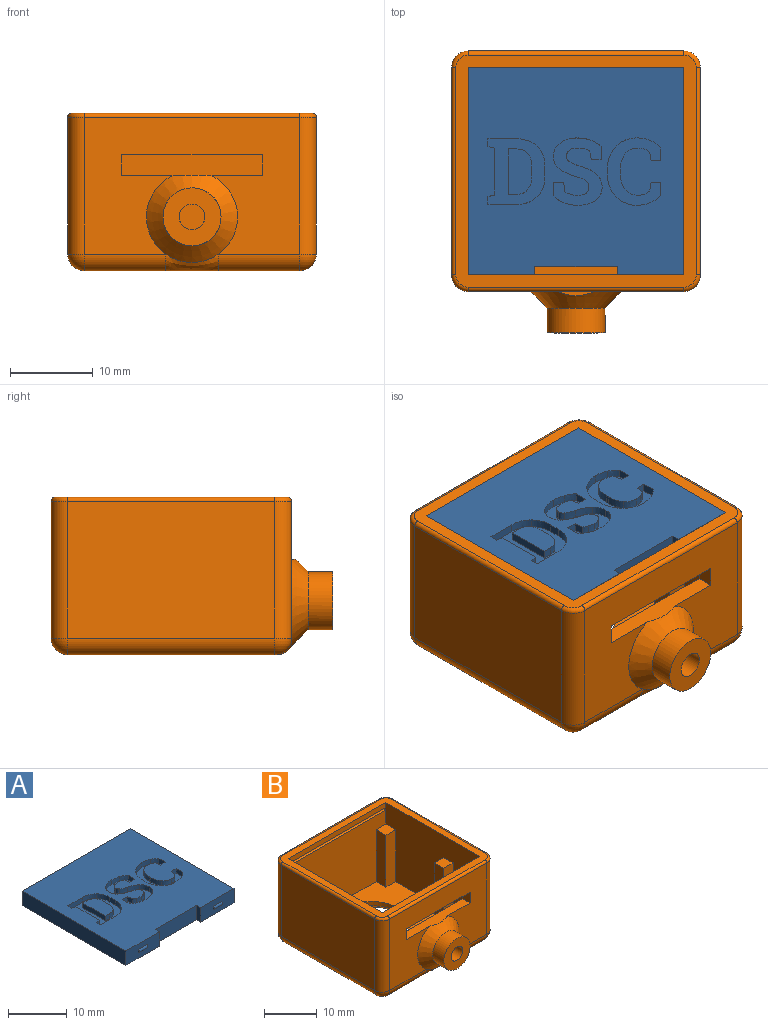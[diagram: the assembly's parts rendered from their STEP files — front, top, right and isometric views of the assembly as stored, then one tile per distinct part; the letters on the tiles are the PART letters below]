
ASSEMBLY  parts=2 mates=1
PART A: 100 faces, bbox 26x25.6x3 mm
  f0: plane 26x25mm, normal (0,0,1), area 544.6mm2, adj f1,f2,f3,f4,f5,f6,f7,f8
  f1: plane 3x1mm, normal (1,0,0), area 3mm2, adj f0,f2,f8,f9
  f2: plane 10x3mm, normal (0,-1,0), area 30mm2, adj f0,f1,f3,f9
  f3: plane 3x1mm, normal (-1,0,0), area 3mm2, adj f0,f2,f4,f9
  f4: plane 8x3mm, normal (0,-1,0), area 22.8mm2, adj f0,f3,f5,f9,f97,f98,f99
  f5: plane 25x3mm, normal (1,0,0), area 75mm2, adj f0,f4,f6,f9
  f6: plane 26x3mm, normal (0,1,0), area 69.6mm2, adj f0,f5,f7,f9,f88,f89,f90,f91
  f7: plane 25x3mm, normal (-1,0,0), area 75mm2, adj f0,f6,f8,f9
  f8: plane 8x3mm, normal (0,-1,0), area 22.8mm2, adj f0,f1,f7,f9,f94,f95,f96
  f9: plane 26x25mm, normal (0,0,-1), area 640mm2, adj f1,f2,f3,f4,f5,f6,f7,f8
  f10: plane 1.62x1mm, normal (-1,0,0), area 1.6mm2, adj f0,f11,f39,f40
  f11: extruded ~1.26x1mm, area 1.5mm2, adj f0,f10,f12,f40
  f12: extruded ~1.66x1mm, area 1.7mm2, adj f0,f11,f13,f40
  f13: extruded ~2.05x1mm, area 2.2mm2, adj f0,f12,f14,f40
  f14: extruded ~1.57x1mm, area 1.8mm2, adj f0,f13,f15,f40
  f15: extruded ~1.53x1mm, area 1.8mm2, adj f0,f14,f16,f40
  f16: extruded ~2.13x1mm, area 2.4mm2, adj f0,f15,f17,f40
  f17: extruded ~1.13x1mm, area 1.3mm2, adj f0,f16,f18,f40
  f18: extruded ~1x0.73mm, area 0.8mm2, adj f0,f17,f19,f40
  f19: extruded ~1x0.71mm, area 0.8mm2, adj f0,f18,f20,f40
  f20: extruded ~1x0.99mm, area 1mm2, adj f0,f19,f21,f40
  f21: extruded ~1x0.92mm, area 0.9mm2, adj f0,f20,f22,f40
  f22: extruded ~1x0.65mm, area 0.7mm2, adj f0,f21,f23,f40
  f23: plane 1.12x1mm, normal (-0.99,-0.15,0), area 1.1mm2, adj f0,f22,f24,f40
  f24: plane 1.23x1mm, normal (0,-1,0), area 1.2mm2, adj f0,f23,f25,f40
  f25: plane 1.65x1mm, normal (1,0,0), area 1.6mm2, adj f0,f24,f26,f40
  f26: extruded ~1.26x1mm, area 1.5mm2, adj f0,f25,f27,f40
  f27: extruded ~1.7x1mm, area 1.7mm2, adj f0,f26,f28,f40
  f28: extruded ~2.12x1mm, area 2.2mm2, adj f0,f27,f29,f40
  f29: extruded ~1.6x1mm, area 1.9mm2, adj f0,f28,f30,f40
  f30: extruded ~1.57x1mm, area 1.8mm2, adj f0,f29,f31,f40
  f31: extruded ~1.98x1mm, area 2.2mm2, adj f0,f30,f32,f40
  f32: extruded ~1.28x1mm, area 1.4mm2, adj f0,f31,f33,f40
  f33: extruded ~1x0.66mm, area 0.8mm2, adj f0,f32,f34,f40
  f34: extruded ~1x0.71mm, area 0.8mm2, adj f0,f33,f35,f40
  f35: extruded ~1.01x1mm, area 1.1mm2, adj f0,f34,f36,f40
  f36: extruded ~1x0.84mm, area 0.8mm2, adj f0,f35,f37,f40
  f37: extruded ~1x0.6mm, area 0.6mm2, adj f0,f36,f38,f40
  f38: plane 1.09x1mm, normal (0.98,0.19,0), area 1.1mm2, adj f0,f37,f39,f40
  f39: plane 1.19x1mm, normal (0,1,0), area 1.2mm2, adj f0,f10,f38,f40
  f40: plane 8.12x5.89mm, normal (0,0,1), area 26.6mm2, adj f10,f11,f12,f13,f14,f15,f16,f17
  f41: plane 1.56x1mm, normal (-1,0,0), area 1.6mm2, adj f0,f42,f64,f65
  f42: extruded ~1.22x1mm, area 1.5mm2, adj f0,f41,f43,f65
  f43: extruded ~1.65x1mm, area 1.7mm2, adj f0,f42,f44,f65
  f44: extruded ~2.61x1.11mm, area 2.9mm2, adj f0,f43,f45,f65
  f45: extruded ~2.83x1.01mm, area 3.1mm2, adj f0,f44,f46,f65
  f46: plane 1x0.27mm, normal (1,0,0), area 0.3mm2, adj f0,f45,f47,f65
  f47: extruded ~2.83x1.01mm, area 3.1mm2, adj f0,f46,f48,f65
  f48: extruded ~2.6x1.1mm, area 2.9mm2, adj f0,f47,f49,f65
  f49: extruded ~1.66x1mm, area 1.7mm2, adj f0,f48,f50,f65
  f50: extruded ~1.22x1mm, area 1.5mm2, adj f0,f49,f51,f65
  f51: plane 1.56x1mm, normal (-1,0,0), area 1.6mm2, adj f0,f50,f52,f65
  f52: plane 1.18x1mm, normal (0,-1,0), area 1.2mm2, adj f0,f51,f53,f65
  f53: plane 1.05x1mm, normal (0.99,-0.15,0), area 1.1mm2, adj f0,f52,f54,f65
  f54: extruded ~1x0.6mm, area 0.7mm2, adj f0,f53,f55,f65
  f55: extruded ~1x0.85mm, area 0.9mm2, adj f0,f54,f56,f65
  f56: extruded ~1.56x1mm, area 1.8mm2, adj f0,f55,f57,f65
  f57: extruded ~1.96x1mm, area 2.1mm2, adj f0,f56,f58,f65
  f58: plane 1x0.28mm, normal (-1,0,0), area 0.3mm2, adj f0,f57,f59,f65
  f59: extruded ~1.95x1mm, area 2.1mm2, adj f0,f58,f60,f65
  f60: extruded ~1.59x1mm, area 1.8mm2, adj f0,f59,f61,f65
  f61: extruded ~1x0.84mm, area 0.9mm2, adj f0,f60,f62,f65
  f62: extruded ~1x0.59mm, area 0.7mm2, adj f0,f61,f63,f65
  f63: plane 1.05x1mm, normal (0.99,0.15,0), area 1.1mm2, adj f0,f62,f64,f65
  f64: plane 1.18x1mm, normal (0,1,0), area 1.2mm2, adj f0,f41,f63,f65
  f65: plane 8.13x6.49mm, normal (0,0,1), area 23.7mm2, adj f41,f42,f43,f44,f45,f46,f47,f48
  f66: plane 3.55x1mm, normal (0,-1,0), area 3.6mm2, adj f0,f67,f85,f86
  f67: plane 1x0.96mm, normal (1,0,0), area 1mm2, adj f0,f66,f68,f86
  f68: plane 1x0.84mm, normal (0.19,0.98,0), area 0.9mm2, adj f0,f67,f69,f86
  f69: plane 5.67x1mm, normal (1,0,0), area 5.7mm2, adj f0,f68,f70,f86
  f70: plane 1x0.84mm, normal (0.19,-0.98,0), area 0.9mm2, adj f0,f69,f71,f86
  f71: plane 1x0.95mm, normal (1,0,0), area 0.9mm2, adj f0,f70,f72,f86
  f72: plane 3.55x1mm, normal (0,1,0), area 3.6mm2, adj f0,f71,f73,f86
  f73: extruded ~2.39x1mm, area 2.6mm2, adj f0,f72,f74,f86
  f74: extruded ~2.37x1mm, area 2.6mm2, adj f0,f73,f75,f86
  f75: plane 1.31x1mm, normal (-1,0,0), area 1.3mm2, adj f0,f74,f76,f86
  f76: extruded ~2.37x1mm, area 2.6mm2, adj f0,f75,f85,f86
  f77: plane 1.05x1mm, normal (0,1,0), area 1mm2, adj f78,f84,f86,f87
  f78: extruded ~1.34x1mm, area 1.5mm2, adj f77,f79,f86,f87
  f79: extruded ~1.49x1mm, area 1.6mm2, adj f78,f80,f86,f87
  f80: plane 1.32x1mm, normal (1,0,0), area 1.3mm2, adj f79,f81,f86,f87
  f81: extruded ~1.5x1mm, area 1.6mm2, adj f80,f82,f86,f87
  f82: extruded ~1.34x1mm, area 1.5mm2, adj f81,f83,f86,f87
  f83: plane 1.05x1mm, normal (0,-1,0), area 1mm2, adj f82,f84,f86,f87
  f84: plane 5.46x1mm, normal (-1,0,0), area 5.5mm2, adj f77,f83,f86,f87
  f85: extruded ~2.39x1mm, area 2.6mm2, adj f0,f66,f76,f86
  f86: plane 7.9x6.88mm, normal (0,0,1), area 30.9mm2, adj f66,f67,f68,f69,f70,f71,f72,f73
  f87: plane 5.46x2.86mm, normal (0,0,1), area 14.2mm2, adj f77,f78,f79,f80,f81,f82,f83,f84
  f88: plane 0.6x0.3mm, normal (1,0,0), area 0.1mm2, adj f6,f90
  f89: plane 0.6x0.3mm, normal (-1,0,0), area 0.1mm2, adj f6,f90
  f90: cylinder r=0.3mm len=7mm, axis (-1,0,0), area 6.6mm2, adj f6,f88,f89
  f91: plane 0.6x0.3mm, normal (1,0,0), area 0.1mm2, adj f6,f93
  f92: plane 0.6x0.3mm, normal (-1,0,0), area 0.1mm2, adj f6,f93
  f93: cylinder r=0.3mm len=7mm, axis (-1,0,0), area 6.6mm2, adj f6,f91,f92
  f94: plane 0.6x0.3mm, normal (1,0,0), area 0.1mm2, adj f8,f96
  f95: plane 0.6x0.3mm, normal (-1,0,0), area 0.1mm2, adj f8,f96
  f96: cylinder r=0.3mm len=2mm, axis (-1,0,0), area 1.9mm2, adj f8,f94,f95
  f97: plane 0.6x0.3mm, normal (1,0,0), area 0.1mm2, adj f4,f99
  f98: plane 0.6x0.3mm, normal (-1,0,0), area 0.1mm2, adj f4,f99
  f99: cylinder r=0.3mm len=2mm, axis (-1,0,0), area 1.9mm2, adj f4,f97,f98
PART B: 68 faces, bbox 30.7x34.5x19.4 mm
  f0: plane 26x15.2mm, normal (0,1,0), area 326.1mm2, adj f3,f4,f12,f28,f29,f30,f31,f33
  f1: plane 26x1.2mm, normal (0,1,0), area 31.2mm2, adj f4,f6,f12,f33
  f2: plane 26x1.2mm, normal (0,-1,0), area 31.2mm2, adj f4,f6,f12,f32
  f3: plane 26x25mm, normal (0,0,1), area 458.9mm2, adj f0,f4,f5,f12,f13,f14,f15,f17
  f4: plane 25.6x17mm, normal (-1,0,0), area 364.1mm2, adj f0,f1,f2,f3,f5,f6,f15,f16
  f5: plane 26x15.2mm, normal (0,-1,0), area 332.8mm2, adj f3,f4,f12,f14,f16,f17,f19,f32
  f6: plane 29x28mm, normal (0,0,1), area 160.1mm2, adj f1,f2,f4,f12,f60,f61,f62,f63
  f7: plane 26x16.5mm, normal (0,1,0), area 429mm2, adj f52,f56,f58,f60
  f8: plane 25x16.5mm, normal (-1,0,0), area 412.5mm2, adj f49,f55,f58,f63
  f9: plane 26x16.5mm, normal (0,-1,0), area 297.3mm2, adj f28,f29,f30,f31,f44,f45,f46,f49
  f10: plane 25x16.5mm, normal (1,0,0), area 412.5mm2, adj f46,f51,f52,f64
  f11: plane 26x25.27mm, normal (0,0,-1), area 437mm2, adj f45,f47,f50,f51,f55,f56,f59
  f12: plane 25.6x17mm, normal (1,0,0), area 364.1mm2, adj f0,f1,f2,f3,f5,f6,f18,f19
  f13: cylinder r=7.25mm len=14.5mm, axis (0,0,-1), area 45.6mm2, adj f3,f59
  f14: plane 12x2.6mm, normal (-1,0,0), area 31.2mm2, adj f3,f5,f15,f16
  f15: plane 12x2.6mm, normal (0,-1,0), area 31.2mm2, adj f3,f4,f14,f16
  f16: plane 2.6x2.6mm, normal (0,0,1), area 6.8mm2, adj f4,f5,f14,f15
  f17: plane 12x2.6mm, normal (1,0,0), area 31.2mm2, adj f3,f5,f18,f19
  f18: plane 12x2.6mm, normal (0,-1,0), area 31.2mm2, adj f3,f12,f17,f19
  f19: plane 2.6x2.6mm, normal (0,0,1), area 6.8mm2, adj f5,f12,f17,f18
  f20: plane 12x2.5mm, normal (0,-1,0), area 30mm2, adj f3,f12,f21,f23
  f21: plane 12x2.5mm, normal (1,0,0), area 30mm2, adj f3,f20,f22,f23
  f22: plane 12x2.5mm, normal (0,1,0), area 30mm2, adj f3,f12,f21,f23
  f23: plane 2.5x2.5mm, normal (0,0,1), area 6.2mm2, adj f12,f20,f21,f22
  f24: plane 12x2.5mm, normal (0,-1,0), area 30mm2, adj f3,f4,f26,f27
  f25: plane 12x2.5mm, normal (0,1,0), area 30mm2, adj f3,f4,f26,f27
  f26: plane 12x2.5mm, normal (-1,0,0), area 30mm2, adj f3,f24,f25,f27
  f27: plane 2.5x2.5mm, normal (0,0,1), area 6.2mm2, adj f4,f24,f25,f26
  f28: plane 2.5x2mm, normal (1,0,0), area 5mm2, adj f0,f9,f29,f31
  f29: plane 17x2mm, normal (0,0,-1), area 34mm2, adj f0,f9,f28,f30
  f30: plane 2.5x2mm, normal (-1,0,0), area 5mm2, adj f0,f9,f29,f31
  f31: plane 17.36x2.87mm, normal (0,0,1), area 35.5mm2, adj f0,f9,f28,f30,f44
  f32: cylinder r=0.3mm len=26mm, axis (-1,0,0), area 24.5mm2, adj f2,f4,f5,f12
  f33: cylinder r=0.3mm len=26mm, axis (-1,0,0), area 24.5mm2, adj f0,f1,f4,f12
  f34: cylinder r=3.5mm len=7mm, axis (0,1,0), area 66mm2, adj f35,f44
  f35: plane 7x7mm, normal (0,-1,0), area 30.9mm2, adj f34,f36
  f36: cylinder r=1.55mm len=5mm, axis (0,1,0), area 48.7mm2, adj f35,f43
  f37: plane 3.2x2mm, normal (1,0,0), area 6.4mm2, adj f0,f38,f42,f43
  f38: plane 2.77x2mm, normal (0.5,0,-0.87), area 6.4mm2, adj f0,f37,f39,f43
  f39: plane 2.77x2mm, normal (-0.5,0,-0.87), area 6.4mm2, adj f0,f38,f40,f43
  f40: plane 3.2x2mm, normal (-1,0,0), area 6.4mm2, adj f0,f39,f41,f43
  f41: plane 2.77x2mm, normal (-0.5,0,0.87), area 6.4mm2, adj f0,f40,f42,f43
  f42: plane 2.77x2mm, normal (0.5,0,0.87), area 6.4mm2, adj f0,f37,f41,f43
  f43: plane 6.39x5.55mm, normal (0,1,0), area 19.1mm2, adj f36,f37,f38,f39,f40,f41,f42
  f44: cone r=3.5mm half-angle=45deg, axis (0,1,0), area 78.4mm2, adj f9,f31,f34,f47
  f45: cylinder r=2mm len=9.84mm, axis (1,0,0), area 30.9mm2, adj f9,f11,f47,f48
  f46: cylinder r=2mm len=16.5mm, axis (0,0,1), area 51.8mm2, adj f9,f10,f48,f66
  f47: bspline ~6.32x2mm, area 15.5mm2, adj f11,f44,f45,f50
  f48: sphere r=2mm, area 6.3mm2, adj f45,f46,f51
  f49: cylinder r=2mm len=16.5mm, axis (0,0,-1), area 51.8mm2, adj f8,f9,f53,f65
  f50: cylinder r=2mm len=9.84mm, axis (1,0,0), area 30.9mm2, adj f9,f11,f47,f53
  f51: cylinder r=2mm len=25mm, axis (0,1,0), area 78.5mm2, adj f10,f11,f48,f54
  f52: cylinder r=2mm len=16.5mm, axis (0,0,-1), area 51.8mm2, adj f7,f10,f54,f62
  f53: sphere r=2mm, area 6.3mm2, adj f49,f50,f55
  f54: sphere r=2mm, area 6.3mm2, adj f51,f52,f56
  f55: cylinder r=2mm len=25mm, axis (0,-1,0), area 78.5mm2, adj f8,f11,f53,f57
  f56: cylinder r=2mm len=26mm, axis (-1,0,0), area 81.7mm2, adj f7,f11,f54,f57
  f57: sphere r=2mm, area 6.3mm2, adj f55,f56,f58
  f58: cylinder r=2mm len=16.5mm, axis (0,0,1), area 51.8mm2, adj f7,f8,f57,f61
  f59: cone r=7.25mm half-angle=45deg, axis (0,0,-1), area 68.9mm2, adj f11,f13
  f60: cylinder r=0.5mm len=26mm, axis (1,0,0), area 20.4mm2, adj f6,f7,f61,f62
  f61: torus R=1.5mm, axis (0,0,1), area 2.2mm2, adj f6,f58,f60,f63
  f62: torus R=1.5mm, axis (0,0,1), area 2.2mm2, adj f6,f52,f60,f64
  f63: cylinder r=0.5mm len=25mm, axis (0,1,0), area 19.6mm2, adj f6,f8,f61,f65
  f64: cylinder r=0.5mm len=25mm, axis (0,-1,0), area 19.6mm2, adj f6,f10,f62,f66
  f65: torus R=1.5mm, axis (0,0,1), area 2.2mm2, adj f6,f49,f63,f67
  f66: torus R=1.5mm, axis (0,0,1), area 2.2mm2, adj f6,f46,f64,f67
  f67: cylinder r=0.5mm len=26mm, axis (-1,0,0), area 20.4mm2, adj f6,f9,f65,f66
PLACE A t=(-31.9,0,-10.7)mm
PLACE B t=(-31.9,0,-26.7)mm fixed
MATE fastened B.f32 <-> A.f90  axis (1,0,0) through (-44.9,12.5,-9.2)mm
